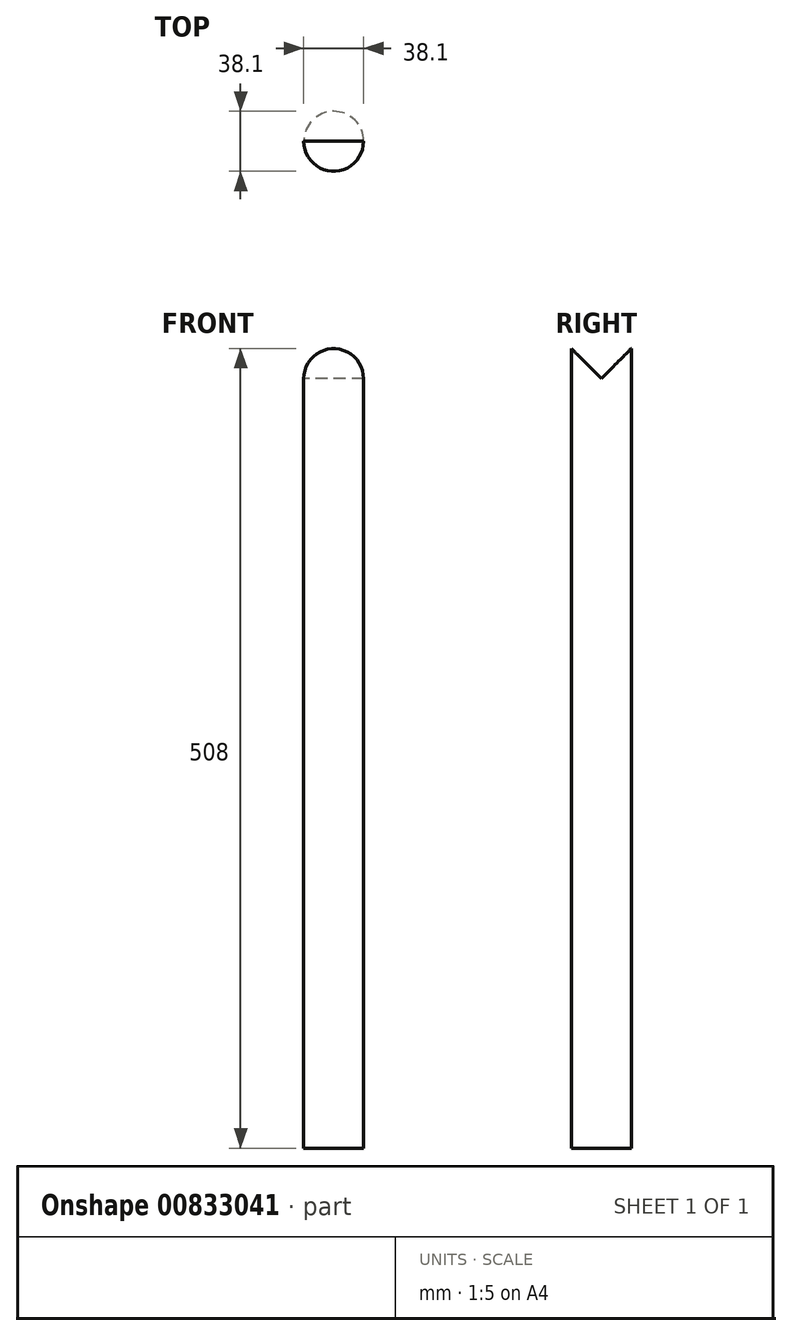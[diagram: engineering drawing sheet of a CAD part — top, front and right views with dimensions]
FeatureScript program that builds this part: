
annotation { "Feature Type Name" : "Feature", "Feature Type Description" : "" }
export const myFeature = defineFeature(function(context is Context, id is Id, definition is map)
    precondition{}
    {
        {
            var Q0;
            Q0=qCreatedBy(makeId("Top.planeOp"),FACE);
            var sketch = newSketch(context, id + "F0", { "sketchPlane" : qUnion([Q0])});
            skCircle(sketch, "E0", {"center": v(0, 0) * mm, "radius": 19.05 * mm});
            skSolve(sketch);
        }
        {
            var Q0;
            Q0 = qSketchRegion(id + "F0", true);
            var Q1;
            Q1=makeQuery(id+"F0.imprint","IMPRINT",FACE,{"disambiguationData":[TD([[makeQuery(id+"F0.imprint","IMPRINT",EDGE,{"derivedFrom":sQuery(id+"F0.wireOp",EDGE,"E0")}),1.0]])]});
            extrude(context, id + "F1", {"entities" : qUnion([Q0, Q1]), "depth" : 508 * mm, "offsetDistance" : 25.4 * mm});
        }
        {
            var Q0;
            Q0=makeQuery(id+"F1.opExtrude","CAP_FACE",FACE,{"disambiguationData":[OSD([sQuery(id+"F0.wireOp",EDGE,"E0")])],"isStart":false});
            var sketch = newSketch(context, id + "F2", { "sketchPlane" : qUnion([Q0])});
            skPoint(sketch, "E1", {"position": v(15.78, -10.67) * mm});
            skSolve(sketch);
        }
        {
            var Q0;
            Q0=makeQuery(id+"F1.opExtrude","CAP_EDGE",EDGE,{"disambiguationData":[OSD([sQuery(id+"F0.wireOp",EDGE,"E0")])],"isStart":false});
            cPlane(context, id + "F3", {"entities" : qUnion([Q0]), "cplaneType" : CPlaneType.LINE_ANGLE, "offset" : 25.4 * mm, "angle" : 0 * degree, "width" : 152.4 * mm, "height" : 152.4 * mm});
        }
        {
            var Q0;
            Q0=qCreatedBy(id+"F3.planeOp",FACE);
            var sketch = newSketch(context, id + "F4", { "sketchPlane" : qUnion([Q0])});
            skLineSegment(sketch, "E2.0", {"start": v(-19.05, 508) * mm, "end": v(19.05, 508) * mm});
            skLineSegment(sketch, "E3", {"start": v(-19.05, 508) * mm, "end": v(0, 488.95) * mm});
            skLineSegment(sketch, "E4", {"start": v(0, 488.95) * mm, "end": v(19.05, 508) * mm});
            skSolve(sketch);
        }
        {
            var Q0;
            Q0 = qSketchRegion(id + "F4", true);
            extrude(context, id + "F5", {"entities" : qUnion([Q0]), "operationType" : NewBodyOperationType.REMOVE, "depth" : 25.4 * mm, "offsetDistance" : 25.4 * mm, "hasSecondDirection" : true, "secondDirectionOppositeDirection" : true, "secondDirectionDepth" : 25.4 * mm});
        }
    });
